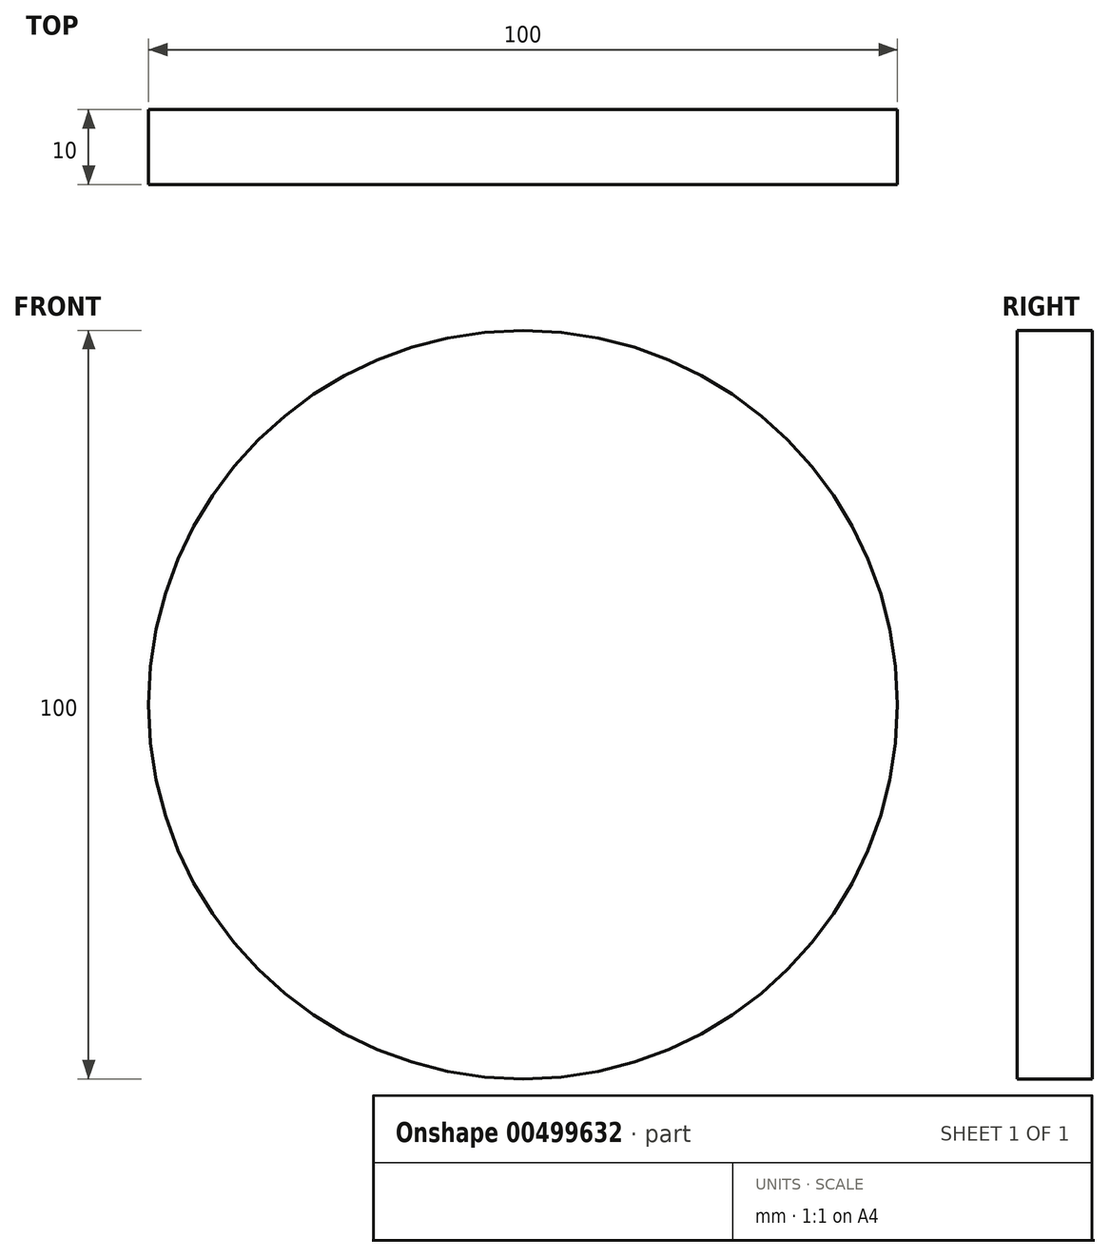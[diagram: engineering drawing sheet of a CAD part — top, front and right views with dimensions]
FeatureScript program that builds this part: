
annotation { "Feature Type Name" : "Feature", "Feature Type Description" : "" }
export const myFeature = defineFeature(function(context is Context, id is Id, definition is map)
    precondition{}
    {
        {
            var Q0;
            Q0=qCreatedBy(makeId("Front.planeOp"),FACE);
            var sketch = newSketch(context, id + "F0", { "sketchPlane" : qUnion([Q0])});
            skLineSegment(sketch, "E0.top", {"start": v(0, 80) * mm, "end": v(66.17, 80) * mm});
            skCircle(sketch, "E1", {"center": v(0, 0) * mm, "radius": 50 * mm});
            skSolve(sketch);
        }
        {
            var Q0;
            Q0=makeQuery(id+"F0.imprint","IMPRINT",FACE,{"disambiguationData":[TD([[makeQuery(id+"F0.imprint","IMPRINT",EDGE,{"derivedFrom":sQuery(id+"F0.wireOp",EDGE,"E1")}),1.0]])]});
            extrude(context, id + "F1", {"entities" : qUnion([Q0]), "depth" : 10 * mm});
        }
    });
